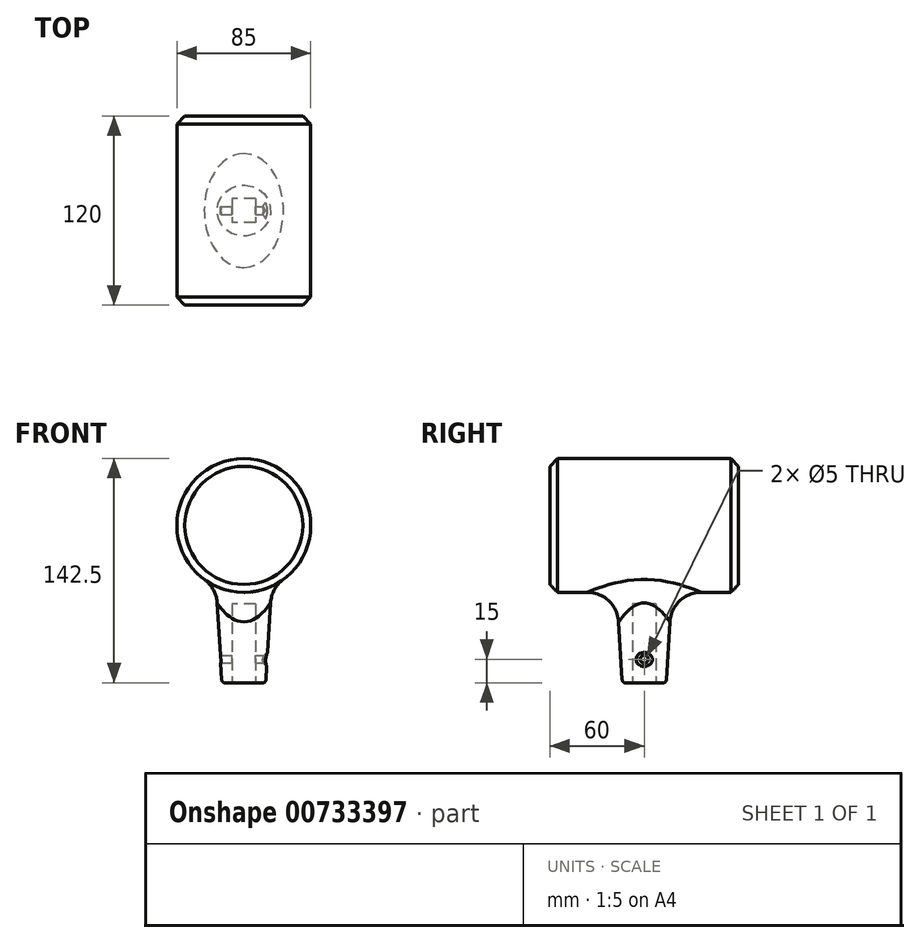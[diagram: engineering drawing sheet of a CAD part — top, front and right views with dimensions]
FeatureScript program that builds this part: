
annotation { "Feature Type Name" : "Feature", "Feature Type Description" : "" }
export const myFeature = defineFeature(function(context is Context, id is Id, definition is map)
    precondition{}
    {
        {
            var Q0;
            Q0=qCreatedBy(makeId("Front.planeOp"),FACE);
            var sketch = newSketch(context, id + "F0", { "sketchPlane" : qUnion([Q0])});
            skCircle(sketch, "E0", {"center": v(0, 0) * mm, "radius": 42.5 * mm});
            skSolve(sketch);
        }
        {
            var Q0;
            Q0=makeQuery(id+"F0.imprint","IMPRINT",FACE,{"disambiguationData":[TD([[makeQuery(id+"F0.imprint","IMPRINT",EDGE,{"derivedFrom":sQuery(id+"F0.wireOp",EDGE,"E0")}),1.0]])]});
            extrude(context, id + "F1", {"entities" : qUnion([Q0]), "endBound" : BoundingType.SYMMETRIC, "depth" : 120 * mm, "offsetDistance" : 25 * mm});
        }
        {
            var Q0;
            Q0=qCreatedBy(makeId("Top.planeOp"),FACE);
            var sketch = newSketch(context, id + "F2", { "sketchPlane" : qUnion([Q0])});
            skCircle(sketch, "E1", {"center": v(0, 0) * mm, "radius": 20 * mm});
            skSolve(sketch);
        }
        {
            var Q0;
            Q0 = qSketchRegion(id + "F2", true);
            extrude(context, id + "F3", {"entities" : qUnion([Q0]), "operationType" : NewBodyOperationType.ADD, "oppositeDirection" : true, "depth" : 100 * mm, "offsetDistance" : 25 * mm, "hasDraft" : true, "draftAngle" : 3.5 * degree, "draftPullDirection" : true});
        }
        {
            var Q0;
            Q0=makeQuery(id+"F3.opExtrude","CAP_FACE",FACE,{"disambiguationData":[OSD([sQuery(id+"F2.wireOp",EDGE,"E1")])],"isStart":false});
            var sketch = newSketch(context, id + "F4", { "sketchPlane" : qUnion([Q0])});
            skLineSegment(sketch, "E2.bottom", {"start": v(7.5, -7.5) * mm, "end": v(-7.5, -7.5) * mm});
            skLineSegment(sketch, "E2.top", {"start": v(7.5, 7.5) * mm, "end": v(-7.5, 7.5) * mm});
            skLineSegment(sketch, "E2.left", {"start": v(7.5, -7.5) * mm, "end": v(7.5, 7.5) * mm});
            skLineSegment(sketch, "E2.right", {"start": v(-7.5, -7.5) * mm, "end": v(-7.5, 7.5) * mm});
            skPoint(sketch, "E2.middle", {"position": v(0, 0) * mm});
            skSolve(sketch);
        }
        {
            var Q0;
            Q0 = qSketchRegion(id + "F4", true);
            extrude(context, id + "F5", {"entities" : qUnion([Q0]), "operationType" : NewBodyOperationType.REMOVE, "oppositeDirection" : true, "depth" : 50 * mm, "offsetDistance" : 25 * mm});
        }
        {
            var Q0;
            Q0=qCreatedBy(makeId("Right.planeOp"),FACE);
            var sketch = newSketch(context, id + "F6", { "sketchPlane" : qUnion([Q0])});
            skCircle(sketch, "E3", {"center": v(0, -85) * mm, "radius": 2.5 * mm});
            skSolve(sketch);
        }
        {
            var Q0;
            Q0 = qSketchRegion(id + "F6", true);
            extrude(context, id + "F7", {"entities" : qUnion([Q0]), "operationType" : NewBodyOperationType.REMOVE, "endBound" : BoundingType.SYMMETRIC, "oppositeDirection" : true, "depth" : 100 * mm, "offsetDistance" : 25 * mm});
        }
        {
            var Q0;
            Q0=makeQuery(id+"F1.opExtrude","CAP_FACE",FACE,{"disambiguationData":[OSD([sQuery(id+"F0.wireOp",EDGE,"E0")])],"isStart":false});
            var Q1;
            Q1=makeQuery(id+"F1.opExtrude","CAP_FACE",FACE,{"disambiguationData":[OSD([sQuery(id+"F0.wireOp",EDGE,"E0")])],"isStart":true});
            chamfer(context, id + "F8", {"entities" : qUnion([Q0, Q1]), "width" : 5 * mm, "tangentPropagation" : true});
        }
        {
            var Q0;
            Q0=makeQuery(id+"F3.boolean.opBoolean","INTERSECT",EDGE,{"derivedFrom":[makeQuery(id+"F1.opExtrude","SWEPT_FACE",FACE,{"disambiguationData":[OSD([sQuery(id+"F0.wireOp",EDGE,"E0")])]}),makeQuery(id+"F3.opExtrude","SWEPT_FACE",FACE,{"disambiguationData":[OSD([sQuery(id+"F2.wireOp",EDGE,"E1")])]})]});
            fillet(context, id + "F9", {"entities" : qUnion([Q0]), "radius" : 20 * mm, "tangentPropagation" : true, "allowEdgeOverflow" : false});
        }
        {
            var Q0;
            Q0=makeQuery(id+"F3.opExtrude","CAP_EDGE",EDGE,{"disambiguationData":[OSD([sQuery(id+"F2.wireOp",EDGE,"E1")])],"isStart":false});
            fillet(context, id + "F10", {"entities" : qUnion([Q0]), "radius" : 2 * mm, "tangentPropagation" : true, "allowEdgeOverflow" : false});
        }
        {
            var Q0;
            Q0=makeQuery(id+"F7.boolean.opBoolean","INTERSECT",EDGE,{"disambiguationData":[OD(0.0)],"derivedFrom":[makeQuery(id+"F3.opExtrude","SWEPT_FACE",FACE,{"disambiguationData":[OSD([sQuery(id+"F2.wireOp",EDGE,"E1")])]}),makeQuery(id+"F7.opExtrude","SWEPT_FACE",FACE,{"disambiguationData":[OSD([sQuery(id+"F6.wireOp",EDGE,"E3")])]})]});
            chamfer(context, id + "F11", {"entities" : qUnion([Q0]), "width" : 2 * mm, "tangentPropagation" : true});
        }
    });
